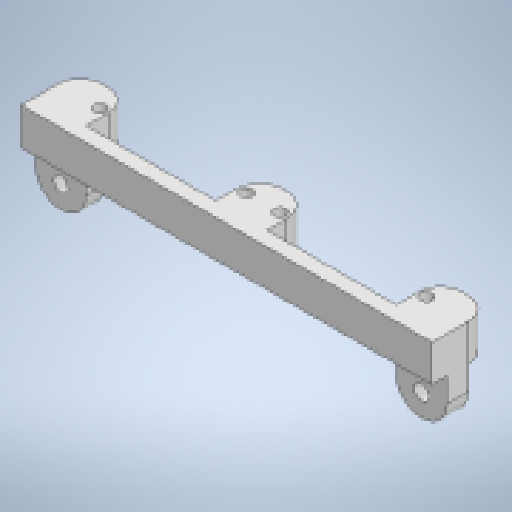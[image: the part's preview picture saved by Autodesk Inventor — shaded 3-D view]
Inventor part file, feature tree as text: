
AUTODESK INVENTOR PART (.ipt)
format: ipt  version: 2023 (Build 270158000, 158)  size: 352,768 bytes
history: native  units: in
note: dims shown in document units (in); Inventor stores cm internally (conversion verified against a paired STEP export)
features: reference x17, other x14, sketch x10, extrude x10, projected_geometry x9, fillet x3
ambient origin geometry x8: Origin, YZ Plane, XZ Plane, XY Plane, X Axis, Y Axis, Z Axis, Center Point
bodies: Body1 (feature_tree)
feature tree (63):
  other  "Bryła1"
  sketch  "Szkic1"
  other  "Płaszczyzna konstrukcyjna1"
  extrude  "Wyciągnięcie proste1"  Depth=0.0394in
  sketch  "Szkic2"
  other  "Płaszczyzna konstrukcyjna2"
  extrude  "Wyciągnięcie proste2"  Depth=0.0394in
  extrude  "Wyciągnięcie proste3"  Depth=0.0394in
  other  "Edytuj bezpośrednio1"
  sketch  "Szkic4"
  other  "Płaszczyzna konstrukcyjna3"
  extrude  "Wyciągnięcie proste4"  Depth=0.3937in TaperAngle=0.0deg
  other  "Edytuj bezpośrednio2"
  extrude  "Wyciągnięcie proste5"  Depth=0.3937in TaperAngle=0.0deg
  extrude  "Wyciągnięcie proste6"  Depth=0.1969in TaperAngle=0.0deg
  extrude  "Wyciągnięcie proste7"  TaperAngle=0.0deg  [1 undecoded]
  extrude  "Wyciągnięcie proste8"  Depth=0.1969in TaperAngle=0.0deg
  fillet  "Zaokrąglenie1"  [1 undecoded]
  fillet  "Zaokrąglenie2"  Radius=0.1181in
  fillet  "Zaokrąglenie3"  [1 undecoded]
  extrude  "Wyciągnięcie proste9"  Depth=0.3937in TaperAngle=0.0deg
  extrude  "Wyciągnięcie proste10"  TaperAngle=0.0deg  [1 undecoded]
  reference  "Odniesienie1"
  reference  "Odniesienie2"
  reference  "Odniesienie3"
  reference  "Odniesienie4"
  reference  "Odniesienie5"
  reference  "Odniesienie6"
  reference  "Odniesienie7"
  reference  "Odniesienie8"
  reference  "Odniesienie9"
  reference  "Odniesienie10"
  reference  "Odniesienie11"
  projected_geometry  "Pętla rzutowana1"
  projected_geometry  "Pętla rzutowana2"
  projected_geometry  "Pętla rzutowana3"
  sketch  "Szkic3"
  projected_geometry  "Pętla rzutowana4"
  reference  "Odniesienie12"
  sketch  "Szkic5"
  sketch  "Szkic6"
  projected_geometry  "Pętla rzutowana5"
  sketch  "Szkic7"
  projected_geometry  "Pętla rzutowana6"
  sketch  "Szkic8"
  projected_geometry  "Pętla rzutowana7"
  projected_geometry  "Pętla rzutowana8"
  sketch  "Szkic9"
  projected_geometry  "Pętla rzutowana9"
  reference  "Odniesienie13"
  reference  "Odniesienie14"
  reference  "Odniesienie15"
  reference  "Odniesienie16"
  sketch  "Szkic10"
  reference  "Odniesienie17"
  other  "servo_stefan_MIR:1"
  other  "servo_stefan:1"
  other  "SCIANA_2.0_MIR:1"
  other  "SCIANA_2.0:1"
  other  "opona_nowa:1"
  other  "Przesuń1"
  other  "bateria szczurza:1"
  other  "Przesuń2"
note: 4 required parameter values undecoded (feature->parameter linkage not recoverable at this tier; creation-order binding heuristic only, values carry confidence <= 0.55)
